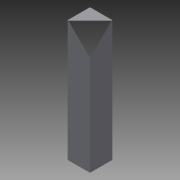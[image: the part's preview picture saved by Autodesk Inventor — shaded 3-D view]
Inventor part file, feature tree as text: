
AUTODESK INVENTOR PART (.ipt)
format: ipt  version: 2015 (Build 190159000, 159)  size: 68,096 bytes
history: native  units: in
note: dims shown in document units (in); Inventor stores cm internally (conversion verified against a paired STEP export)
features: extrude x1, sketch x1
ambient origin geometry x8: Origin, YZ Plane, XZ Plane, XY Plane, X Axis, Y Axis, Z Axis, Center Point
bodies: Solid1 (feature_tree)
feature tree (2):
  extrude  "Extrusion1"  Depth=0.75in
  sketch  "Sketch1"  dims[d0=0.75in d1=0.75in d2=4.04in d3=0.0in]
